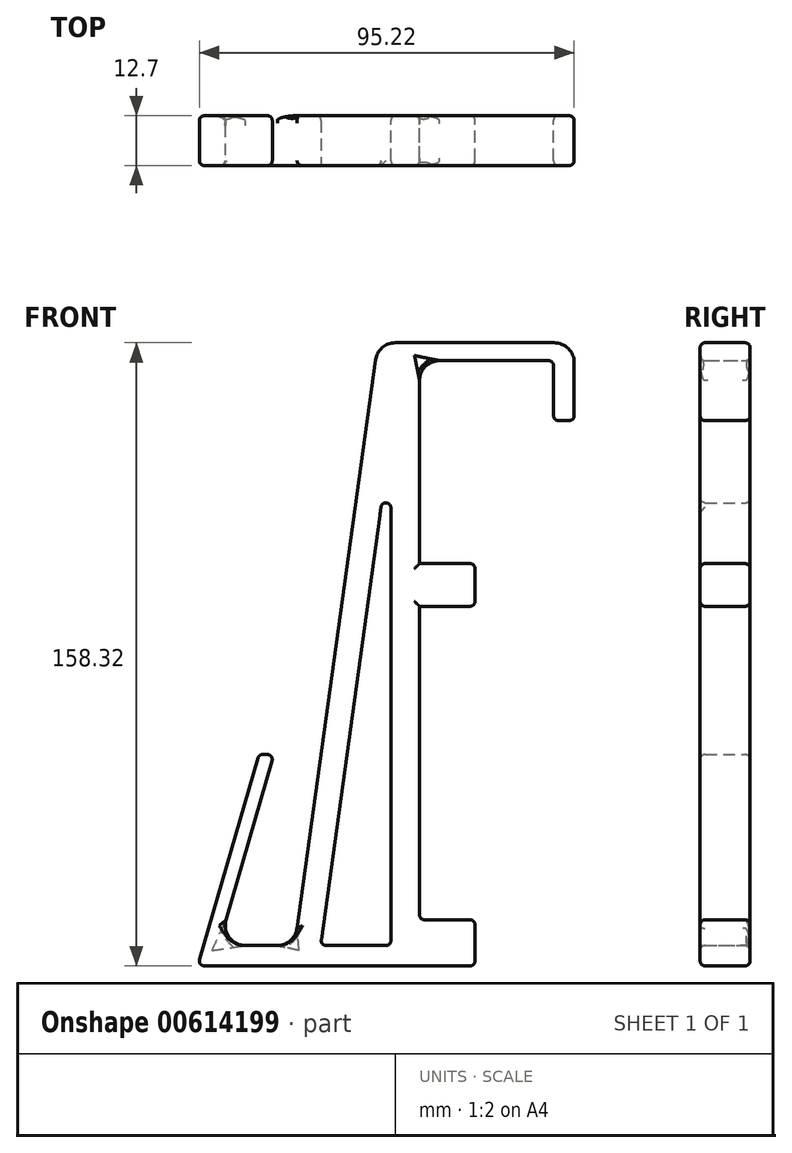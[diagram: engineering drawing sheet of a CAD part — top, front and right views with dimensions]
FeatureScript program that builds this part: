
annotation { "Feature Type Name" : "Feature", "Feature Type Description" : "" }
export const myFeature = defineFeature(function(context is Context, id is Id, definition is map)
    precondition{}
    {
        {
            var Q0;
            Q0=qCreatedBy(makeId("Front.planeOp"),FACE);
            var sketch = newSketch(context, id + "F0", { "sketchPlane" : qUnion([Q0])});
            skLineSegment(sketch, "E0", {"start": v(41.71, 133.36) * mm, "end": v(38.7, 133.36) * mm});
            skLineSegment(sketch, "E1", {"start": v(38.7, 133.36) * mm, "end": v(38.7, 148.62) * mm});
            skLineSegment(sketch, "E2", {"start": v(38.7, 148.62) * mm, "end": v(4.65, 148.62) * mm});
            skLineSegment(sketch, "E3", {"start": v(4.65, 148.62) * mm, "end": v(4.65, 97.04) * mm});
            skLineSegment(sketch, "E4", {"start": v(4.65, -5.16) * mm, "end": v(-51.7, -5.16) * mm});
            skLineSegment(sketch, "E5", {"start": v(-51.7, -5.16) * mm, "end": v(-36.14, 48.54) * mm});
            skLineSegment(sketch, "E6", {"start": v(-36.14, 48.54) * mm, "end": v(-32.33, 48.54) * mm});
            skLineSegment(sketch, "E7", {"start": v(-32.33, 48.54) * mm, "end": v(-46.39, 0) * mm});
            skLineSegment(sketch, "E8", {"start": v(-46.39, 0) * mm, "end": v(-27.04, 0) * mm});
            skLineSegment(sketch, "E9", {"start": v(-27.04, 0) * mm, "end": v(-6.11, 151.7) * mm});
            skLineSegment(sketch, "E10", {"start": v(-20.5, 0) * mm, "end": v(-2.6, 0) * mm});
            skPoint(sketch, "E11.start.orphan", {"position": v(0, 153.16) * mm});
            skLineSegment(sketch, "E12", {"start": v(-2.6, 129.72) * mm, "end": v(-20.5, 0) * mm});
            skLineSegment(sketch, "E13", {"start": v(4.65, 97.04) * mm, "end": v(18.75, 97.04) * mm});
            skLineSegment(sketch, "E14", {"start": v(18.75, 97.04) * mm, "end": v(18.75, 86.2) * mm});
            skLineSegment(sketch, "E15", {"start": v(18.75, 86.2) * mm, "end": v(4.65, 86.2) * mm});
            skLineSegment(sketch, "E16.trimOffspring", {"start": v(4.65, 86.2) * mm, "end": v(4.65, 6.56) * mm});
            skPoint(sketch, "E17.orphan", {"position": v(0, 148.62) * mm});
            skPoint(sketch, "E18.orphan", {"position": v(-5.91, 153.16) * mm});
            skLineSegment(sketch, "E19", {"start": v(4.65, 6.56) * mm, "end": v(18.75, 6.56) * mm});
            skLineSegment(sketch, "E20", {"start": v(18.75, 6.56) * mm, "end": v(18.75, -5.16) * mm});
            skLineSegment(sketch, "E21", {"start": v(18.75, -5.16) * mm, "end": v(4.65, -5.16) * mm});
            skLineSegment(sketch, "E22", {"start": v(38.7, 133.36) * mm, "end": v(43.94, 133.36) * mm});
            skPoint(sketch, "E22.endSnap0", {"position": v(40.2, 133.36) * mm});
            skLineSegment(sketch, "E23", {"start": v(43.94, 133.36) * mm, "end": v(43.94, 153.16) * mm});
            skLineSegment(sketch, "E24", {"start": v(43.94, 153.16) * mm, "end": v(-5.91, 153.16) * mm});
            skLineSegment(sketch, "E25", {"start": v(-6.11, 151.7) * mm, "end": v(-5.91, 153.16) * mm});
            skPoint(sketch, "E26.orphan", {"position": v(0, 129.72) * mm});
            skLineSegment(sketch, "E27", {"start": v(-2.6, 129.72) * mm, "end": v(-2.6, 0) * mm});
            skPoint(sketch, "E28.start.orphan", {"position": v(-1.3, 129.72) * mm});
            skSolve(sketch);
        }
        {
            var Q0;
            Q0=makeQuery(id+"F0.imprint","IMPRINT",FACE,{"disambiguationData":[TD([[makeQuery(id+"F0.imprint","IMPRINT",EDGE,{"derivedFrom":sQuery(id+"F0.wireOp",EDGE,"KnBHMKyh-VmdD-H7sI-4YRO-vwrzje6zqPXn")}),-1.0]])]});
            var Q1;
            {var subQ2=sQuery(id+"F0.wireOp",EDGE,"E1");Q1=makeQuery(id+"F0.imprint","IMPRINT",FACE,{"disambiguationData":[TD([[makeQuery(id+"F0.imprint","IMPRINT",EDGE,{"derivedFrom":subQ2}),-1.0]])]});}
            extrude(context, id + "F1", {"entities" : qUnion([Q0, Q1]), "depth" : 12.7 * mm, "offsetDistance" : 25.4 * mm});
        }
        {
            var Q0;
            Q0=makeQuery(id+"F1.opExtrude","SWEPT_EDGE",EDGE,{"disambiguationData":[OSD([sQuery(id+"F0.wireOp",EDGE,"E12"),sQuery(id+"F0.wireOp",EDGE,"Bk6zNjHY-LAlG-lBTS-agNk-ghVCI7C8jAzF")])]});
            var Q1;
            Q1=makeQuery(id+"F1.opExtrude","CAP_EDGE",EDGE,{"disambiguationData":[OSD([sQuery(id+"F0.wireOp",EDGE,"Bk6zNjHY-LAlG-lBTS-agNk-ghVCI7C8jAzF")])],"isStart":false});
            var Q2;
            Q2=makeQuery(id+"F1.opExtrude","CAP_EDGE",EDGE,{"disambiguationData":[OSD([sQuery(id+"F0.wireOp",EDGE,"E28")])],"isStart":false});
            var Q3;
            Q3=makeQuery(id+"F1.opExtrude","SWEPT_EDGE",EDGE,{"disambiguationData":[OSD([sQuery(id+"F0.wireOp",EDGE,"Bk6zNjHY-LAlG-lBTS-agNk-ghVCI7C8jAzF"),sQuery(id+"F0.wireOp",EDGE,"E28")])]});
            var Q4;
            Q4=makeQuery(id+"F1.opExtrude","CAP_EDGE",EDGE,{"disambiguationData":[OSD([sQuery(id+"F0.wireOp",EDGE,"E27")])],"isStart":false});
            var Q5;
            Q5=makeQuery(id+"F1.opExtrude","CAP_EDGE",EDGE,{"disambiguationData":[OSD([sQuery(id+"F0.wireOp",EDGE,"E3")])],"isStart":false});
            var Q6;
            Q6=makeQuery(id+"F1.opExtrude","CAP_EDGE",EDGE,{"disambiguationData":[OSD([sQuery(id+"F0.wireOp",EDGE,"E3")])],"isStart":true});
            var Q7;
            Q7=makeQuery(id+"F1.opExtrude","CAP_EDGE",EDGE,{"disambiguationData":[OSD([sQuery(id+"F0.wireOp",EDGE,"E2")])],"isStart":false});
            var Q8;
            Q8=makeQuery(id+"F1.opExtrude","CAP_EDGE",EDGE,{"disambiguationData":[OSD([sQuery(id+"F0.wireOp",EDGE,"E23")])],"isStart":false});
            var Q9;
            Q9=makeQuery(id+"F1.opExtrude","CAP_EDGE",EDGE,{"disambiguationData":[OSD([sQuery(id+"F0.wireOp",EDGE,"E22")])],"isStart":false});
            var Q10;
            Q10=makeQuery(id+"F1.opExtrude","SWEPT_EDGE",EDGE,{"disambiguationData":[OSD([sQuery(id+"F0.wireOp",EDGE,"E22"),sQuery(id+"F0.wireOp",EDGE,"E23")])]});
            var Q11;
            Q11=makeQuery(id+"F1.opExtrude","SWEPT_EDGE",EDGE,{"disambiguationData":[OSD([sQuery(id+"F0.wireOp",EDGE,"E1"),sQuery(id+"F0.wireOp",EDGE,"E22")])]});
            var Q12;
            Q12=makeQuery(id+"F1.opExtrude","CAP_EDGE",EDGE,{"disambiguationData":[OSD([sQuery(id+"F0.wireOp",EDGE,"E2")])],"isStart":true});
            var Q13;
            Q13=makeQuery(id+"F1.opExtrude","CAP_EDGE",EDGE,{"disambiguationData":[OSD([sQuery(id+"F0.wireOp",EDGE,"E24")])],"isStart":false});
            var Q14;
            Q14=makeQuery(id+"F1.opExtrude","CAP_FACE",FACE,{"disambiguationData":[OSD([sQuery(id+"F0.wireOp",EDGE,"E1"),sQuery(id+"F0.wireOp",EDGE,"E2"),sQuery(id+"F0.wireOp",EDGE,"E3"),sQuery(id+"F0.wireOp",EDGE,"E4"),sQuery(id+"F0.wireOp",EDGE,"E5"),sQuery(id+"F0.wireOp",EDGE,"E6"),sQuery(id+"F0.wireOp",EDGE,"E7"),sQuery(id+"F0.wireOp",EDGE,"E8"),sQuery(id+"F0.wireOp",EDGE,"E9"),sQuery(id+"F0.wireOp",EDGE,"E10"),sQuery(id+"F0.wireOp",EDGE,"E12"),sQuery(id+"F0.wireOp",EDGE,"E13"),sQuery(id+"F0.wireOp",EDGE,"E14"),sQuery(id+"F0.wireOp",EDGE,"E15"),sQuery(id+"F0.wireOp",EDGE,"E16.trimOffspring"),sQuery(id+"F0.wireOp",EDGE,"E19"),sQuery(id+"F0.wireOp",EDGE,"E20"),sQuery(id+"F0.wireOp",EDGE,"E21"),sQuery(id+"F0.wireOp",EDGE,"E22"),sQuery(id+"F0.wireOp",EDGE,"E23"),sQuery(id+"F0.wireOp",EDGE,"E24"),sQuery(id+"F0.wireOp",EDGE,"E25"),sQuery(id+"F0.wireOp",EDGE,"E27")])],"isStart":true});
            var Q15;
            Q15=makeQuery(id+"F1.opExtrude","SWEPT_EDGE",EDGE,{"disambiguationData":[OSD([sQuery(id+"F0.wireOp",EDGE,"E5"),sQuery(id+"F0.wireOp",EDGE,"E6")])]});
            var Q16;
            Q16=makeQuery(id+"F1.opExtrude","SWEPT_EDGE",EDGE,{"disambiguationData":[OSD([sQuery(id+"F0.wireOp",EDGE,"E6"),sQuery(id+"F0.wireOp",EDGE,"E7")])]});
            var Q17;
            Q17=makeQuery(id+"F1.opExtrude","CAP_EDGE",EDGE,{"disambiguationData":[OSD([sQuery(id+"F0.wireOp",EDGE,"E6")])],"isStart":false});
            var Q18;
            Q18=makeQuery(id+"F1.opExtrude","CAP_EDGE",EDGE,{"disambiguationData":[OSD([sQuery(id+"F0.wireOp",EDGE,"E7")])],"isStart":false});
            var Q19;
            Q19=makeQuery(id+"F1.opExtrude","CAP_EDGE",EDGE,{"disambiguationData":[OSD([sQuery(id+"F0.wireOp",EDGE,"E5")])],"isStart":false});
            var Q20;
            Q20=makeQuery(id+"F1.opExtrude","CAP_EDGE",EDGE,{"disambiguationData":[OSD([sQuery(id+"F0.wireOp",EDGE,"E9"),sQuery(id+"F0.wireOp",EDGE,"E25")])],"isStart":false});
            var Q21;
            Q21=makeQuery(id+"F1.opExtrude","SWEPT_EDGE",EDGE,{"disambiguationData":[OSD([sQuery(id+"F0.wireOp",EDGE,"E13"),sQuery(id+"F0.wireOp",EDGE,"E14")])]});
            var Q22;
            Q22=makeQuery(id+"F1.opExtrude","SWEPT_EDGE",EDGE,{"disambiguationData":[OSD([sQuery(id+"F0.wireOp",EDGE,"E14"),sQuery(id+"F0.wireOp",EDGE,"E15")])]});
            var Q23;
            Q23=makeQuery(id+"F1.opExtrude","CAP_EDGE",EDGE,{"disambiguationData":[OSD([sQuery(id+"F0.wireOp",EDGE,"E14")])],"isStart":false});
            var Q24;
            Q24=makeQuery(id+"F1.opExtrude","CAP_EDGE",EDGE,{"disambiguationData":[OSD([sQuery(id+"F0.wireOp",EDGE,"E13")])],"isStart":false});
            var Q25;
            Q25=makeQuery(id+"F1.opExtrude","CAP_EDGE",EDGE,{"disambiguationData":[OSD([sQuery(id+"F0.wireOp",EDGE,"E15")])],"isStart":false});
            var Q26;
            Q26=makeQuery(id+"F1.opExtrude","CAP_EDGE",EDGE,{"disambiguationData":[OSD([sQuery(id+"F0.wireOp",EDGE,"E16.trimOffspring")])],"isStart":false});
            var Q27;
            Q27=makeQuery(id+"F1.opExtrude","CAP_EDGE",EDGE,{"disambiguationData":[OSD([sQuery(id+"F0.wireOp",EDGE,"E1")])],"isStart":false});
            var Q28;
            Q28=makeQuery(id+"F1.opExtrude","SWEPT_EDGE",EDGE,{"disambiguationData":[OSD([sQuery(id+"F0.wireOp",EDGE,"E10"),sQuery(id+"F0.wireOp",EDGE,"E27")])]});
            var Q29;
            Q29=makeQuery(id+"F1.opExtrude","SWEPT_EDGE",EDGE,{"disambiguationData":[OSD([sQuery(id+"F0.wireOp",EDGE,"E4"),sQuery(id+"F0.wireOp",EDGE,"E5")])]});
            var Q30;
            Q30=makeQuery(id+"F1.opExtrude","CAP_EDGE",EDGE,{"disambiguationData":[OSD([sQuery(id+"F0.wireOp",EDGE,"E19")])],"isStart":false});
            var Q31;
            Q31=makeQuery(id+"F1.opExtrude","CAP_EDGE",EDGE,{"disambiguationData":[OSD([sQuery(id+"F0.wireOp",EDGE,"E20")])],"isStart":false});
            var Q32;
            Q32=makeQuery(id+"F1.opExtrude","CAP_EDGE",EDGE,{"disambiguationData":[OSD([sQuery(id+"F0.wireOp",EDGE,"E4"),sQuery(id+"F0.wireOp",EDGE,"E21")])],"isStart":false});
            var Q33;
            Q33=makeQuery(id+"F1.opExtrude","SWEPT_EDGE",EDGE,{"disambiguationData":[OSD([sQuery(id+"F0.wireOp",EDGE,"E19"),sQuery(id+"F0.wireOp",EDGE,"E20")])]});
            var Q34;
            Q34=makeQuery(id+"F1.opExtrude","SWEPT_EDGE",EDGE,{"disambiguationData":[OSD([sQuery(id+"F0.wireOp",EDGE,"E16.trimOffspring"),sQuery(id+"F0.wireOp",EDGE,"E19")])]});
            var Q35;
            Q35=makeQuery(id+"F1.opExtrude","SWEPT_EDGE",EDGE,{"disambiguationData":[OSD([sQuery(id+"F0.wireOp",EDGE,"E20"),sQuery(id+"F0.wireOp",EDGE,"E21")])]});
            var Q36;
            Q36=makeQuery(id+"F1.opExtrude","SWEPT_EDGE",EDGE,{"disambiguationData":[OSD([sQuery(id+"F0.wireOp",EDGE,"E1"),sQuery(id+"F0.wireOp",EDGE,"E2")])]});
            fillet(context, id + "F2", {"entities" : qUnion([Q0, Q1, Q2, Q3, Q4, Q5, Q6, Q7, Q8, Q9, Q10, Q11, Q12, Q13, Q14, Q15, Q16, Q17, Q18, Q19, Q20, Q21, Q22, Q23, Q24, Q25, Q26, Q27, Q28, Q29, Q30, Q31, Q32, Q33, Q34, Q35, Q36]), "radius" : 1.27 * mm, "tangentPropagation" : true, "allowEdgeOverflow" : false});
        }
        {
            var Q0;
            Q0=makeQuery(id+"F1.opExtrude","SWEPT_EDGE",EDGE,{"disambiguationData":[OSD([sQuery(id+"F0.wireOp",EDGE,"E8"),sQuery(id+"F0.wireOp",EDGE,"E9")])]});
            var Q1;
            Q1=makeQuery(id+"F1.opExtrude","SWEPT_EDGE",EDGE,{"disambiguationData":[OSD([sQuery(id+"F0.wireOp",EDGE,"E7"),sQuery(id+"F0.wireOp",EDGE,"E8")])]});
            var Q2;
            Q2=makeQuery(id+"F1.opExtrude","SWEPT_EDGE",EDGE,{"disambiguationData":[OSD([sQuery(id+"F0.wireOp",EDGE,"E2"),sQuery(id+"F0.wireOp",EDGE,"E3")])]});
            var Q3;
            Q3=makeQuery(id+"F1.opExtrude","SWEPT_EDGE",EDGE,{"disambiguationData":[OSD([sQuery(id+"F0.wireOp",EDGE,"E24"),sQuery(id+"F0.wireOp",EDGE,"E25")])]});
            var Q4;
            Q4=makeQuery(id+"F1.opExtrude","SWEPT_EDGE",EDGE,{"disambiguationData":[OSD([sQuery(id+"F0.wireOp",EDGE,"E23"),sQuery(id+"F0.wireOp",EDGE,"E24")])]});
            fillet(context, id + "F3", {"entities" : qUnion([Q0, Q1, Q2, Q3, Q4]), "radius" : 5.08 * mm, "tangentPropagation" : true, "allowEdgeOverflow" : false});
        }
    });
